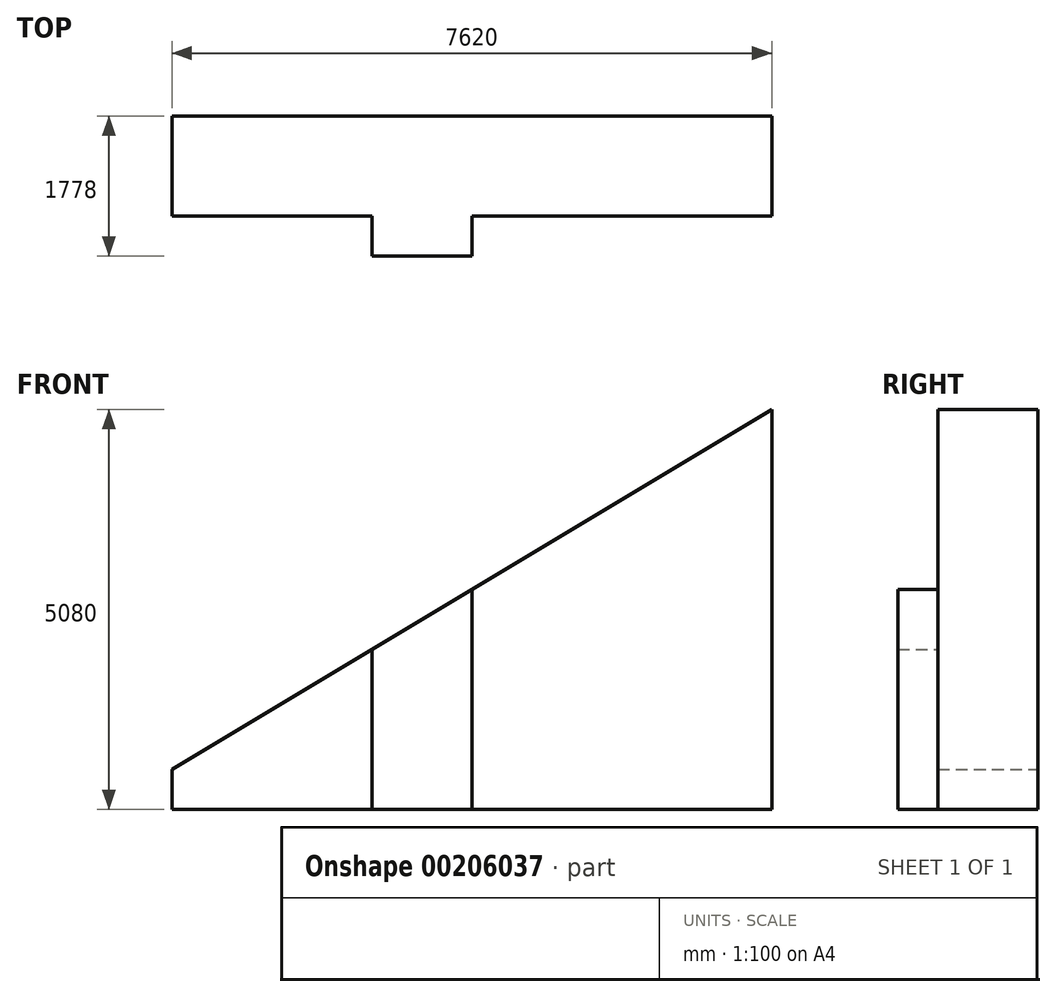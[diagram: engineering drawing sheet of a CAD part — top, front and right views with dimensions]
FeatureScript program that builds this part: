
annotation { "Feature Type Name" : "Feature", "Feature Type Description" : "" }
export const myFeature = defineFeature(function(context is Context, id is Id, definition is map)
    precondition{}
    {
        {
            var Q0;
            Q0=qCreatedBy(makeId("Front.planeOp"),FACE);
            var sketch = newSketch(context, id + "F0", { "sketchPlane" : qUnion([Q0])});
            skLineSegment(sketch, "E0.bottom", {"start": v(-3810, -2540) * mm, "end": v(3810, -2540) * mm});
            skLineSegment(sketch, "E0.top", {"start": v(-3810, 2540) * mm, "end": v(3810, 2540) * mm});
            skLineSegment(sketch, "E0.left", {"start": v(-3810, -2540) * mm, "end": v(-3810, 2540) * mm});
            skLineSegment(sketch, "E0.right", {"start": v(3810, -2540) * mm, "end": v(3810, 2540) * mm});
            skSolve(sketch);
        }
        {
            var Q0;
            Q0=makeQuery(id+"F0.imprint","IMPRINT",FACE,{"disambiguationData":[TD([[makeQuery(id+"F0.imprint","IMPRINT",EDGE,{"derivedFrom":sQuery(id+"F0.wireOp",EDGE,"E0.bottom")}),1.0]])]});
            extrude(context, id + "F1", {"entities" : qUnion([Q0]), "depth" : 1270 * mm});
        }
        {
            var Q0;
            Q0=makeQuery(id+"F1.opExtrude","SWEPT_EDGE",EDGE,{"disambiguationData":[OSD([sQuery(id+"F0.wireOp",EDGE,"E0.top"),sQuery(id+"F0.wireOp",EDGE,"E0.left")])]});
            chamfer(context, id + "F2", {"entities" : qUnion([Q0]), "chamferType" : ChamferType.TWO_OFFSETS, "width1" : 4572 * mm, "oppositeDirection" : false, "width2" : 7620 * mm, "tangentPropagation" : true});
        }
        {
            var Q0;
            Q0=makeQuery(id+"F1.opExtrude","CAP_FACE",FACE,{"disambiguationData":[OSD([sQuery(id+"F0.wireOp",EDGE,"E0.bottom"),sQuery(id+"F0.wireOp",EDGE,"E0.top"),sQuery(id+"F0.wireOp",EDGE,"E0.left"),sQuery(id+"F0.wireOp",EDGE,"E0.right")])],"isStart":false});
            var sketch = newSketch(context, id + "F3", { "sketchPlane" : qUnion([Q0])});
            skLineSegment(sketch, "E1", {"start": v(-1270, -2540) * mm, "end": v(-1270, -508) * mm});
            skLineSegment(sketch, "E2", {"start": v(0, -2540) * mm, "end": v(0, 254) * mm});
            skSolve(sketch);
        }
        {
            var Q0;
            {var subQ0=sQuery(id+"F3.wireOp",EDGE,"E1");Q0=makeQuery(id+"F3.imprint","IMPRINT",FACE,{"disambiguationData":[TD([[makeQuery(id+"F3.imprint","IMPRINT",EDGE,{"derivedFrom":subQ0}),-1.0]])]});}
            extrude(context, id + "F4", {"entities" : qUnion([Q0]), "operationType" : NewBodyOperationType.ADD, "depth" : 508 * mm});
        }
    });
